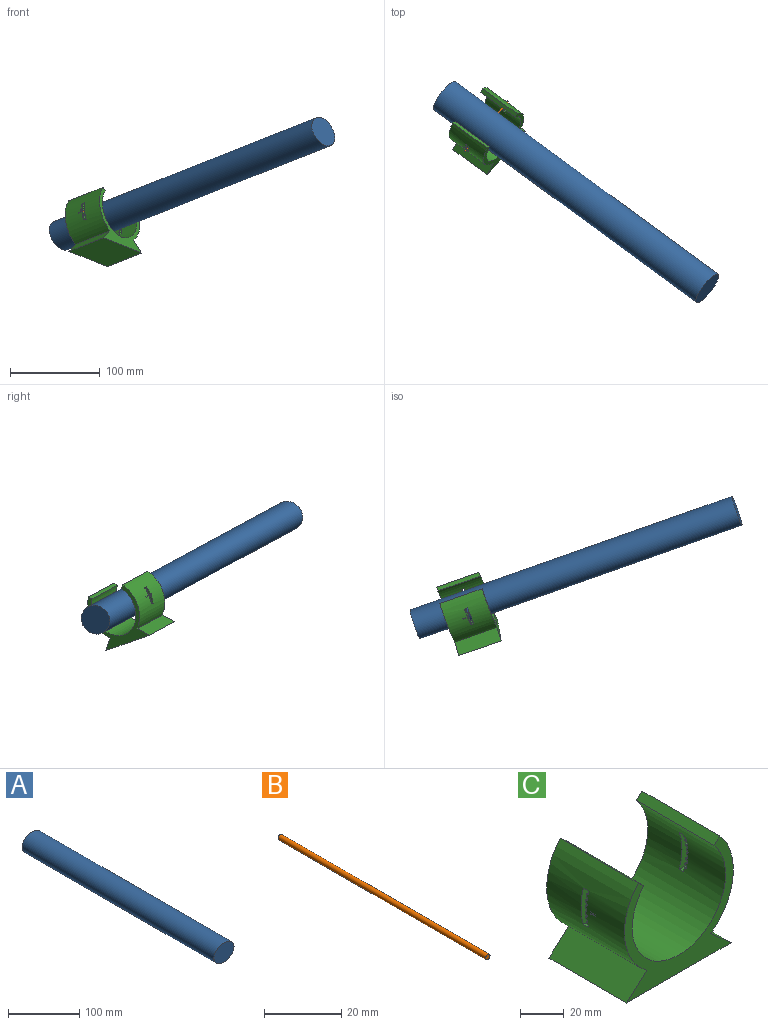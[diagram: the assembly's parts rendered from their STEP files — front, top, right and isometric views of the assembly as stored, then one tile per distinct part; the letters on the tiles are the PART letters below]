
ASSEMBLY  parts=3 mates=3
PART A: 3 faces, bbox 40x381x33 mm
  f0: extruded ~381x40mm, area 43789mm2, adj f1,f2
  f1: plane 40x33mm, normal (0,-1,0), area 1036.7mm2, adj f0
  f2: plane 40x33mm, normal (0,1,0), area 1036.7mm2, adj f0
PART B: 3 faces, bbox 1.6x76.2x1.6 mm
  f0: cylinder r=0.8mm len=76.2mm, axis (0,1,0), area 383mm2, adj f1,f2
  f1: plane 1.6x1.6mm, normal (0,-1,0), area 2mm2, adj f0
  f2: plane 1.6x1.6mm, normal (0,1,0), area 2mm2, adj f0
PART C: 70 faces, bbox 70x50x63.2 mm
  f0: cylinder r=35mm len=51.42mm, axis (0,1,0), area 2840.5mm2, adj f1,f2,f6,f7,f11,f12,f13,f15
  f1: plane 3.12x0.41mm, normal (0,0,-1), area 0.6mm2, adj f0,f3,f31,f62,f63
  f2: plane 3.13x0.41mm, normal (0,0,1), area 0.6mm2, adj f0,f3,f31,f62,f63
  f3: plane 0.93x0.05mm, normal (-1,0,0), area 0mm2, adj f1,f2,f31,f62
  f4: cylinder r=35mm len=51.43mm, axis (0,1,0), area 2841mm2, adj f9,f10,f11,f12,f14,f16,f18,f20
  f5: cylinder r=30mm len=60mm, axis (0,1,0), area 6745.3mm2, adj f6,f10,f11,f12,f13,f14,f15,f16
  f6: plane 50x3.75mm, normal (0.66,0,0.75), area 250mm2, adj f0,f5,f11,f12
  f7: plane 50x12.9mm, normal (-0.67,0,0.74), area 871.6mm2, adj f0,f8,f11,f12
  f8: plane 67.06x50mm, normal (0,0,-1), area 3352.9mm2, adj f7,f9,f11,f12
  f9: plane 50x12.9mm, normal (0.67,0,0.74), area 871.6mm2, adj f4,f8,f11,f12
  f10: plane 50x3.75mm, normal (-0.66,0,0.75), area 250mm2, adj f4,f5,f11,f12
  f11: plane 70x63.15mm, normal (0,-1,0), area 1191.5mm2, adj f0,f4,f5,f6,f7,f8,f9,f10
  f12: plane 70x63.15mm, normal (0,1,0), area 1191.5mm2, adj f0,f4,f5,f6,f7,f8,f9,f10
  f13: cylinder r=0.9mm len=5mm, axis (-1,0,0), area 17.9mm2, adj f0,f5,f47,f53
  f14: cylinder r=0.9mm len=5mm, axis (-1,0,0), area 17.9mm2, adj f4,f5,f46,f52
  f15: cylinder r=0.9mm len=5.14mm, axis (-1,0,0.09), area 17.9mm2, adj f0,f5,f51,f53
  f16: cylinder r=0.9mm len=5.14mm, axis (-1,0,0.09), area 17.9mm2, adj f4,f5,f50,f52
  f17: cylinder r=0.9mm len=5.24mm, axis (-0.98,0,0.17), area 17.9mm2, adj f0,f5,f49,f51
  f18: cylinder r=0.9mm len=5.24mm, axis (-0.98,0,0.17), area 17.9mm2, adj f4,f5,f48,f50
  f19: cylinder r=0.9mm len=5.3mm, axis (-0.97,0,0.26), area 17.9mm2, adj f0,f5,f40,f49
  f20: cylinder r=0.9mm len=5.3mm, axis (-0.97,0,0.26), area 17.9mm2, adj f4,f5,f35,f48
  f21: cylinder r=0.9mm len=5.14mm, axis (-1,0,-0.09), area 17.9mm2, adj f0,f5,f45,f47
  f22: cylinder r=0.9mm len=5.14mm, axis (-1,0,-0.09), area 17.9mm2, adj f4,f5,f44,f46
  f23: cylinder r=0.9mm len=5.24mm, axis (-0.98,0,-0.17), area 17.9mm2, adj f0,f5,f43,f45
  f24: cylinder r=0.9mm len=5.24mm, axis (-0.98,0,-0.17), area 17.9mm2, adj f4,f5,f32,f44
  f25: cylinder r=0.9mm len=5.3mm, axis (-0.97,0,-0.26), area 17.9mm2, adj f0,f5,f38,f43
  f26: cylinder r=0.9mm len=5.3mm, axis (-0.97,0,-0.26), area 17.9mm2, adj f4,f5,f32,f33
  f27: plane 3.12x0.41mm, normal (0,0,-1), area 0.6mm2, adj f4,f28,f30,f54,f55
  f28: plane 0.94x0.41mm, normal (0,1,0), area 0.4mm2, adj f4,f27,f29,f30
  f29: plane 3.11x0.41mm, normal (0,0,1), area 0.6mm2, adj f4,f28,f30,f54,f55
  f30: plane 0.93x0.05mm, normal (1,0,0), area 0mm2, adj f27,f28,f29,f54
  f31: plane 0.94x0.41mm, normal (0,1,0), area 0.4mm2, adj f0,f1,f2,f3
  f32: plane 5.14x2.25mm, normal (0,1,0), area 6mm2, adj f4,f5,f24,f26
  f33: plane 5.31x1.48mm, normal (0,1,0), area 4.4mm2, adj f4,f5,f26,f34
  f34: plane 5.26x2.6mm, normal (0,0,-1), area 13.7mm2, adj f4,f5,f33,f37
  f35: plane 5.44x1.82mm, normal (0,1,0), area 6.2mm2, adj f4,f5,f20,f36
  f36: plane 5.28x2.6mm, normal (0,0,1), area 13.7mm2, adj f4,f5,f35,f37
  f37: plane 20.41x6.85mm, normal (0,-1,0), area 103.8mm2, adj f4,f5,f34,f36
  f38: plane 5.44x1.82mm, normal (0,1,0), area 6.2mm2, adj f0,f5,f25,f39
  f39: plane 5.28x2.6mm, normal (0,0,1), area 13.7mm2, adj f0,f5,f38,f42
  f40: plane 5.31x1.48mm, normal (0,1,0), area 4.4mm2, adj f0,f5,f19,f41
  f41: plane 5.26x2.6mm, normal (0,0,-1), area 13.7mm2, adj f0,f5,f40,f42
  f42: plane 20.41x6.85mm, normal (0,-1,0), area 103.8mm2, adj f0,f5,f39,f41
  f43: plane 5.14x2.25mm, normal (0,1,0), area 6mm2, adj f0,f5,f23,f25
  f44: plane 5.11x1.83mm, normal (0,1,0), area 6mm2, adj f4,f5,f22,f24
  f45: plane 5.11x1.83mm, normal (0,1,0), area 6mm2, adj f0,f5,f21,f23
  f46: plane 5.04x1.41mm, normal (0,1,0), area 6mm2, adj f4,f5,f14,f22
  f47: plane 5.04x1.41mm, normal (0,1,0), area 6mm2, adj f0,f5,f13,f21
  f48: plane 5.14x2.25mm, normal (0,1,0), area 6mm2, adj f4,f5,f18,f20
  f49: plane 5.14x2.25mm, normal (0,1,0), area 6mm2, adj f0,f5,f17,f19
  f50: plane 5.11x1.83mm, normal (0,1,0), area 6mm2, adj f4,f5,f16,f18
  f51: plane 5.11x1.83mm, normal (0,1,0), area 6mm2, adj f0,f5,f15,f17
  f52: plane 5.04x1.41mm, normal (0,1,0), area 6mm2, adj f4,f5,f14,f16
  f53: plane 5.04x1.41mm, normal (0,1,0), area 6mm2, adj f0,f5,f13,f15
  f54: plane 0.93x0.01mm, normal (-0.13,-0.99,0), area 0mm2, adj f27,f29,f30,f55
  f55: plane 3.08x0.94mm, normal (0.99,-0.13,0), area 2.9mm2, adj f4,f27,f29,f54
  f56: plane 0.14x0.04mm, normal (0.99,-0.13,0), area 0mm2, adj f4,f57,f58
  f57: plane 0.13x0mm, normal (0.13,0.99,0), area 0mm2, adj f4,f56,f58
  f58: plane 0.04x0mm, normal (0,0,1), area 0mm2, adj f4,f56,f57
  f59: plane 0.06x0.01mm, normal (0,0,-1), area 0mm2, adj f4,f60,f61
  f60: plane 0.21x0.01mm, normal (0.13,0.99,0), area 0mm2, adj f4,f59,f61
  f61: plane 0.21x0.06mm, normal (0.99,-0.13,0), area 0mm2, adj f4,f59,f60
  f62: plane 0.93x0.01mm, normal (0.13,-0.99,0), area 0mm2, adj f1,f2,f3,f63
  f63: plane 3.08x0.94mm, normal (-0.99,-0.13,0), area 2.9mm2, adj f0,f1,f2,f62
  f64: plane 0.22x0.06mm, normal (-0.99,-0.13,0), area 0mm2, adj f0,f65,f66
  f65: plane 0.21x0.01mm, normal (-0.13,0.99,0), area 0mm2, adj f0,f64,f66
  f66: plane 0.06x0.01mm, normal (0,0,-1), area 0mm2, adj f0,f64,f65
  f67: plane 0.04x0mm, normal (0,0,1), area 0mm2, adj f0,f68,f69
  f68: plane 0.13x0mm, normal (-0.13,0.99,0), area 0mm2, adj f0,f67,f69
  f69: plane 0.14x0.04mm, normal (-0.99,-0.13,0), area 0mm2, adj f0,f67,f68
PLACE A rot(axis=(-0.42,0.11,0.9),56deg) t=(-113.13,-10.19,189.25)mm
PLACE B rot(axis=(-0.46,-0.27,-0.85),45deg) t=(-42.37,-16.62,197.95)mm
PLACE C rot(axis=(-0.06,-0.22,-0.97),129.9deg) t=(-47.41,-58.45,215.31)mm
MATE slider C.f13 <-> B.f0  axis (0.64,0.73,-0.26) through (-88.88,-69.86,216.66)mm
MATE slider A.f1 <-> C.f5  axis (0.77,-0.56,0.3) through (179.39,-225.01,305.22)mm
MATE ball B.f0 <-> C.f4  axis (0.64,0.73,-0.26) through (-66.6,-44.36,207.7)mm
